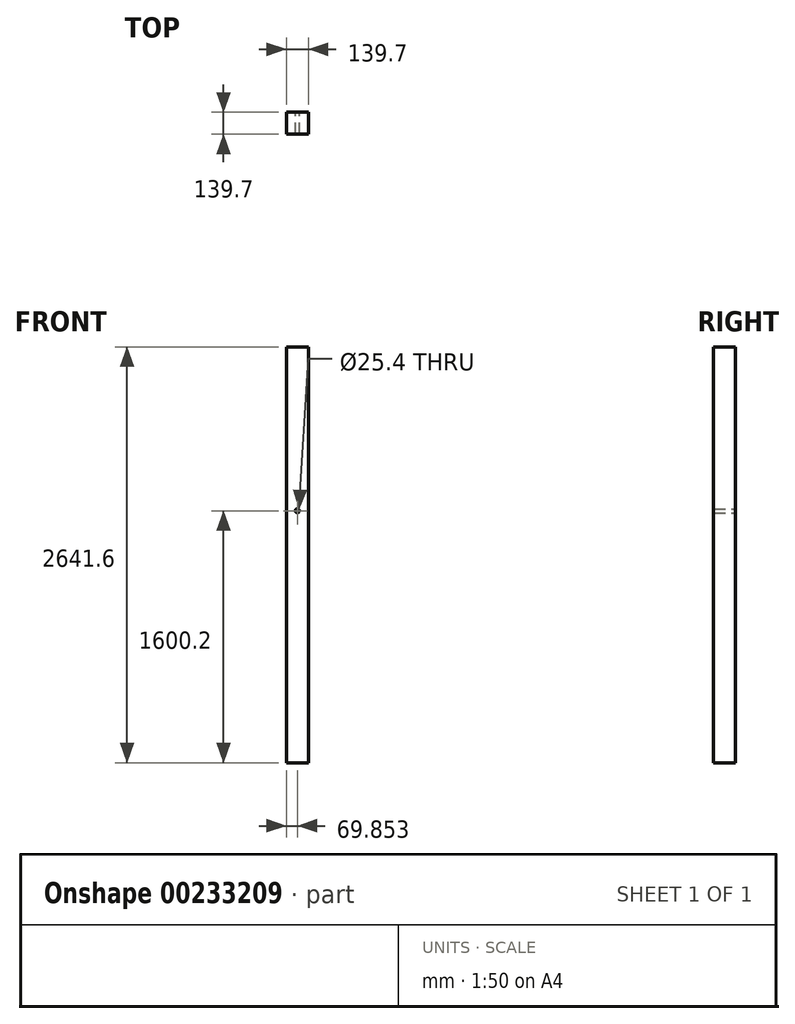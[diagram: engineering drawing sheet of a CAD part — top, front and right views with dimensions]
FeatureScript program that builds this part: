
annotation { "Feature Type Name" : "Feature", "Feature Type Description" : "" }
export const myFeature = defineFeature(function(context is Context, id is Id, definition is map)
    precondition{}
    {
        {
            var Q0;
            Q0=qCreatedBy(makeId("Front.planeOp"),FACE);
            var sketch = newSketch(context, id + "F0", { "sketchPlane" : qUnion([Q0])});
            skLineSegment(sketch, "E0.bottom", {"start": v(-87.03, 2605.11) * mm, "end": v(52.67, 2605.11) * mm});
            skLineSegment(sketch, "E0.top", {"start": v(-87.03, -36.49) * mm, "end": v(52.67, -36.49) * mm});
            skLineSegment(sketch, "E0.left", {"start": v(-87.03, 2605.11) * mm, "end": v(-87.03, -36.49) * mm});
            skLineSegment(sketch, "E0.right", {"start": v(52.67, 2605.11) * mm, "end": v(52.67, -36.49) * mm});
            skCircle(sketch, "E1", {"center": v(-17.18, 1563.71) * mm, "radius": 12.7 * mm});
            skSolve(sketch);
        }
        {
            var Q0;
            Q0 = qSketchRegion(id + "F0", true);
            extrude(context, id + "F1", {"entities" : qUnion([Q0]), "depth" : 139.7 * mm});
        }
    });
